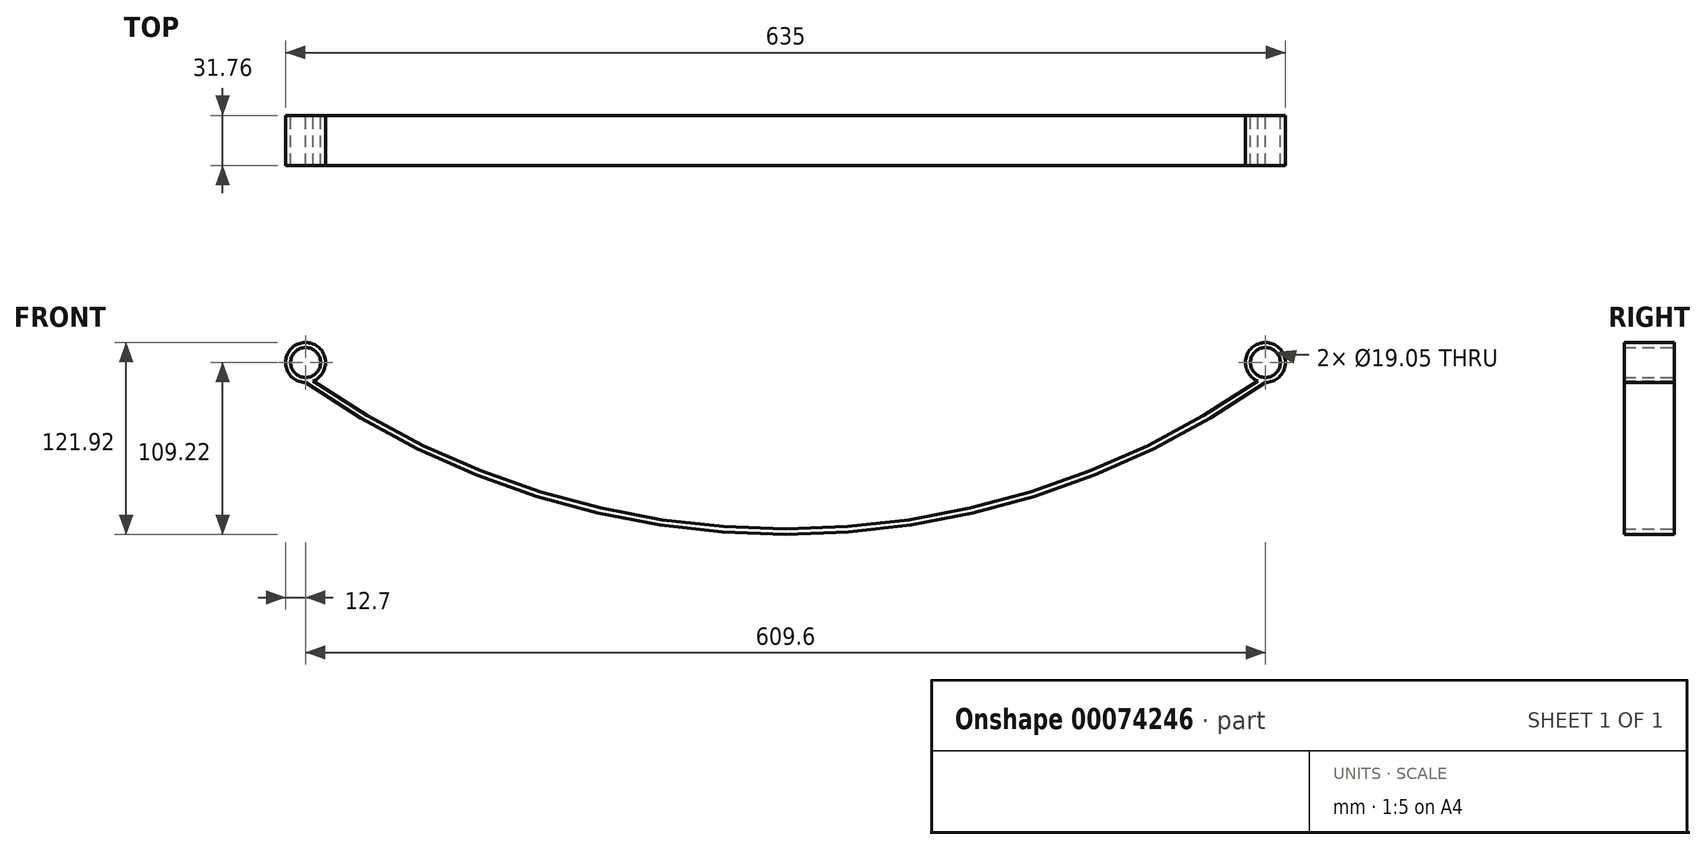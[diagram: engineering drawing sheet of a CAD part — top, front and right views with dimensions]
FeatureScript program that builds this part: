
annotation { "Feature Type Name" : "Feature", "Feature Type Description" : "" }
export const myFeature = defineFeature(function(context is Context, id is Id, definition is map)
    precondition{}
    {
        {
            var Q0;
            Q0=qCreatedBy(makeId("Front.planeOp"),FACE);
            var sketch = newSketch(context, id + "F0", { "sketchPlane" : qUnion([Q0])});
            skLineSegment(sketch, "E0", {"start": v(0, 0) * mm, "end": v(-304.8, 0) * mm, "construction": true});
            skLineSegment(sketch, "E1", {"start": v(0, 0) * mm, "end": v(304.8, 0) * mm, "construction": true});
            skLineSegment(sketch, "E2", {"start": v(0, 0) * mm, "end": v(0, -96.52) * mm, "construction": true});
            skArc(sketch, "E3", {"start": v(-304.8, 0) * mm, "mid": v(0, -96.52) * mm, "end": v(304.8, 0) * mm});
            skCircle(sketch, "E4", {"center": v(-304.8, 12.7) * mm, "radius": 12.7 * mm});
            skPoint(sketch, "E4.second.point", {"position": v(-304.8, 25.4) * mm});
            skPoint(sketch, "E4.third.point", {"position": v(-305.94, 0.05) * mm});
            skCircle(sketch, "E5", {"center": v(-304.8, 12.7) * mm, "radius": 9.53 * mm});
            skCircle(sketch, "E6.MirrorC", {"center": v(304.8, 12.7) * mm, "radius": 12.7 * mm});
            skCircle(sketch, "E7.MirrorC", {"center": v(304.8, 12.7) * mm, "radius": 9.53 * mm});
            skArc(sketch, "E8.0", {"start": v(-300.08, 0.9) * mm, "mid": v(0, -93.07) * mm, "end": v(300.08, 0.9) * mm});
            skLineSegment(sketch, "E9", {"start": v(0, -93.07) * mm, "end": v(0, -96.52) * mm});
            skSolve(sketch);
        }
        {
            var Q0;
            Q0 = qSketchRegion(id + "F0", true);
            extrude(context, id + "F1", {"entities" : qUnion([Q0]), "endBound" : BoundingType.SYMMETRIC, "depth" : 31.75 * mm});
        }
        {
            var Q0;
            Q0=qCreatedBy(makeId("Front.planeOp"),FACE);
            var sketch = newSketch(context, id + "F2", { "sketchPlane" : qUnion([Q0])});
            skArc(sketch, "E10.0", {"start": v(-300.08, 0.9) * mm, "mid": v(0, -93.07) * mm, "end": v(300.08, 0.9) * mm});
            skLineSegment(sketch, "E11.0", {"start": v(0, 0) * mm, "end": v(0, -96.52) * mm, "construction": true});
            skPoint(sketch, "E12", {"position": v(0, -93.07) * mm});
            skSolve(sketch);
        }
        {
            var Q0;
            Q0=sQuery(id+"F2.wireOp",VERTEX,"E11.0.end");
            var Q1;
            Q1=sQuery(id+"F2.wireOp",EDGE,"E11.0");
            cPlane(context, id + "F3", {"entities" : qUnion([Q0, Q1]), "cplaneType" : CPlaneType.LINE_POINT, "offset" : 152.4 * mm, "width" : 152.4 * mm, "height" : 152.4 * mm});
        }
    });
